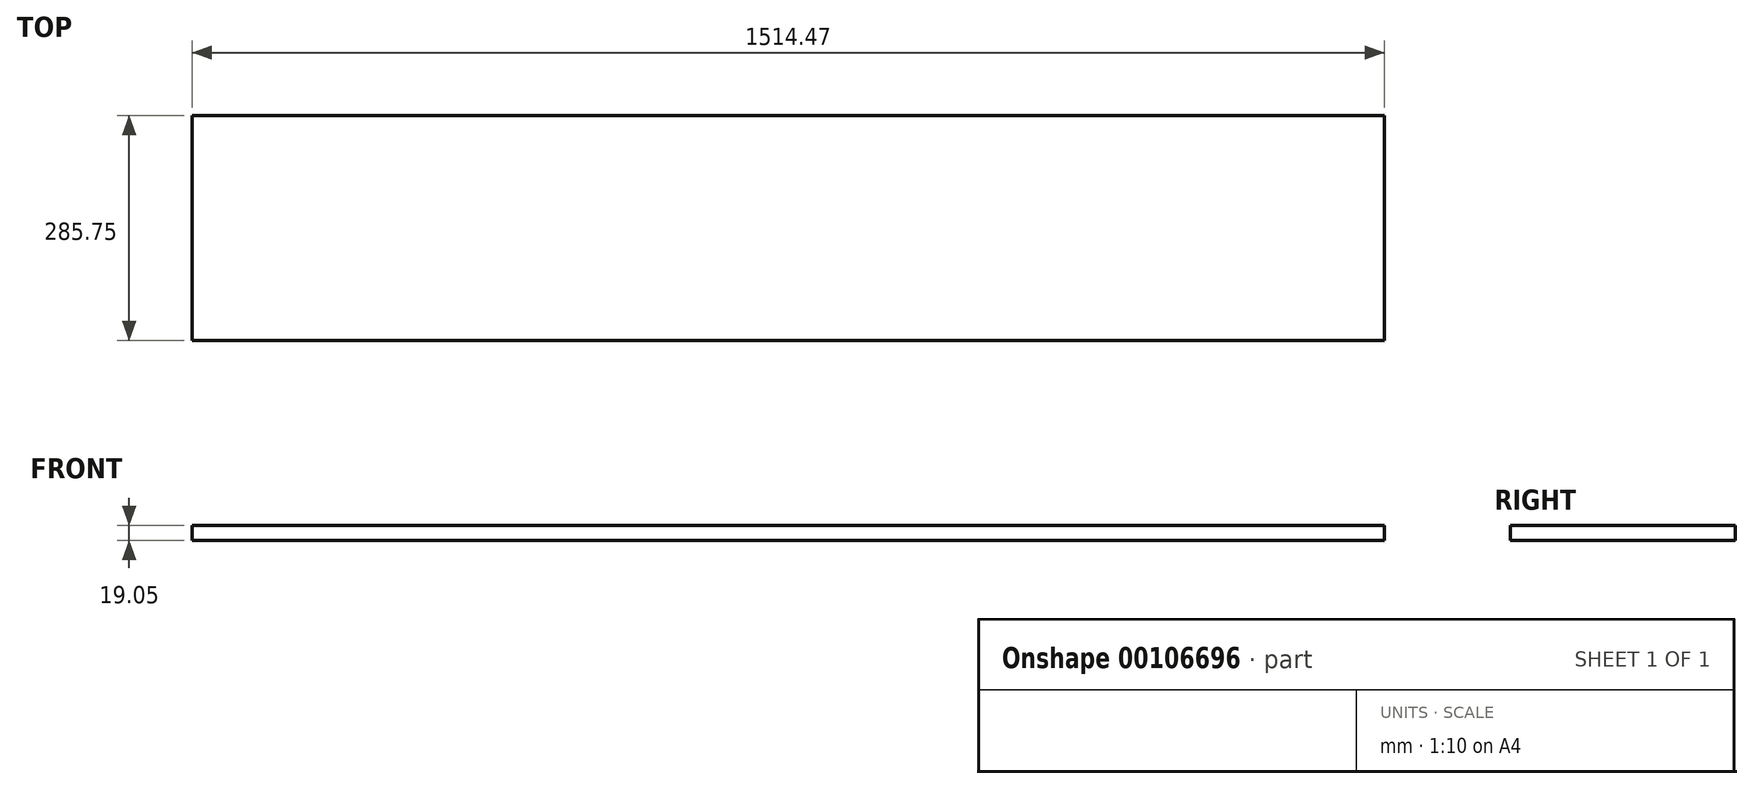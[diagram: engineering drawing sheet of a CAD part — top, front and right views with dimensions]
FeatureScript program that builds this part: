
annotation { "Feature Type Name" : "Feature", "Feature Type Description" : "" }
export const myFeature = defineFeature(function(context is Context, id is Id, definition is map)
    precondition{}
    {
        {
            var Q0;
            Q0=qCreatedBy(makeId("Top.planeOp"),FACE);
            var sketch = newSketch(context, id + "F0", { "sketchPlane" : qUnion([Q0])});
            skLineSegment(sketch, "E0.bottom", {"start": v(0, 0) * mm, "end": v(1514.47, 0) * mm});
            skLineSegment(sketch, "E0.top", {"start": v(0, 285.75) * mm, "end": v(1514.47, 285.75) * mm});
            skLineSegment(sketch, "E0.left", {"start": v(0, 0) * mm, "end": v(0, 285.75) * mm});
            skLineSegment(sketch, "E0.right", {"start": v(1514.48, 0) * mm, "end": v(1514.48, 285.75) * mm});
            skSolve(sketch);
        }
        {
            var Q0;
            Q0=makeQuery(id+"F0.imprint","IMPRINT",FACE,{"disambiguationData":[TD([[makeQuery(id+"F0.imprint","IMPRINT",EDGE,{"derivedFrom":sQuery(id+"F0.wireOp",EDGE,"E0.bottom")}),1.0]])]});
            extrude(context, id + "F1", {"entities" : qUnion([Q0]), "depth" : 19.05 * mm});
        }
    });
